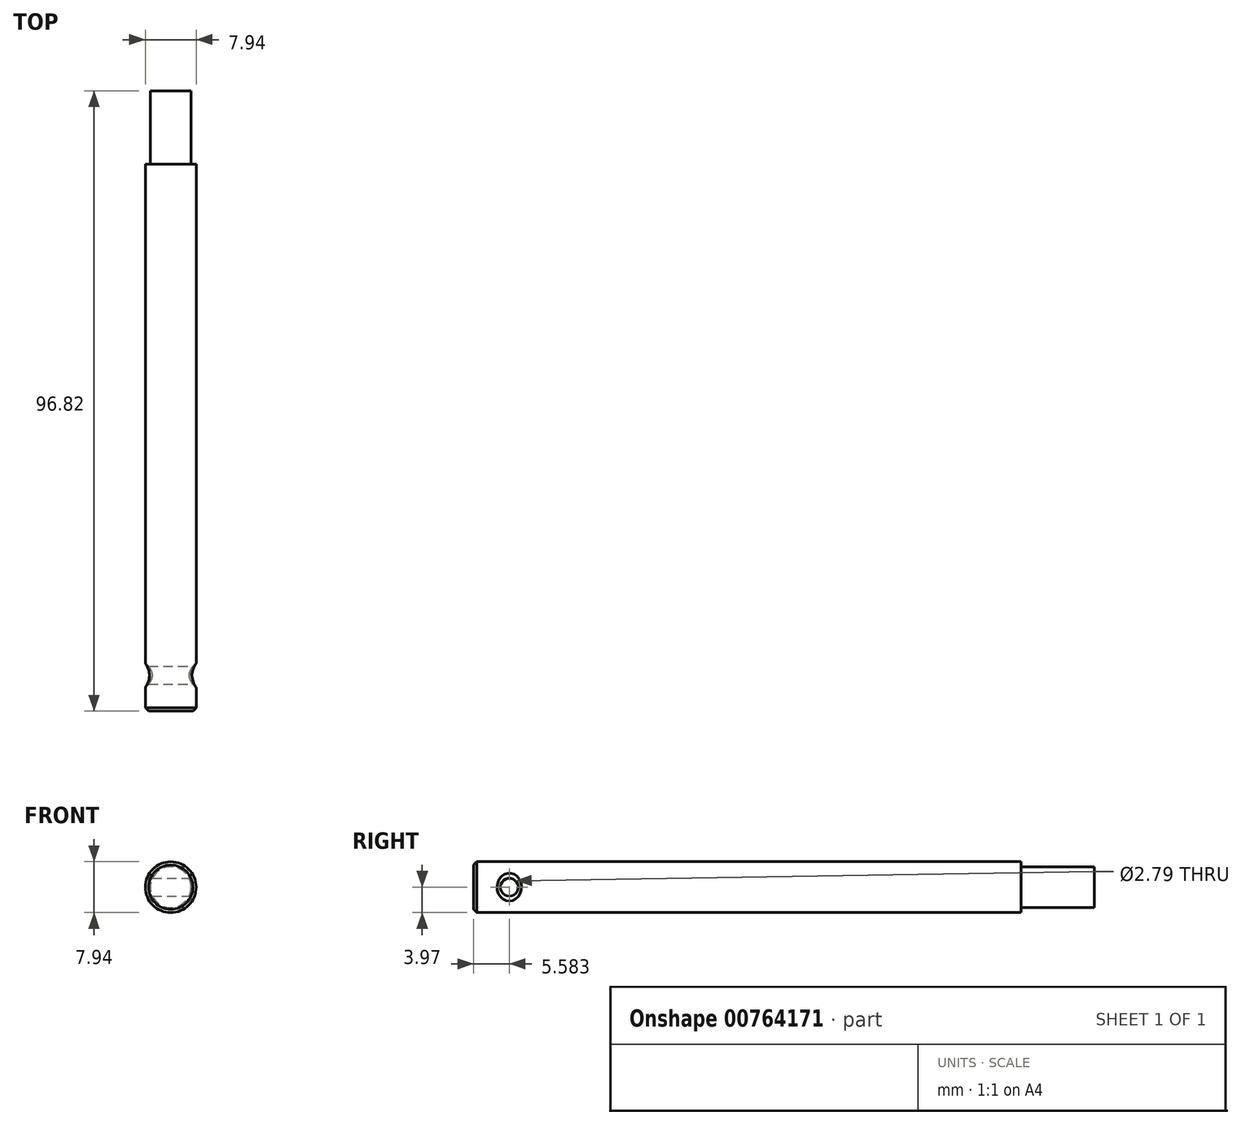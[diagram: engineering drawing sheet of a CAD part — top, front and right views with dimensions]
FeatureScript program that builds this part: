
annotation { "Feature Type Name" : "Feature", "Feature Type Description" : "" }
export const myFeature = defineFeature(function(context is Context, id is Id, definition is map)
    precondition{}
    {
        {
            var Q0;
            Q0=qCreatedBy(makeId("Front.planeOp"),FACE);
            var sketch = newSketch(context, id + "F0", { "sketchPlane" : qUnion([Q0])});
            skCircle(sketch, "E0", {"center": v(0, 0) * mm, "radius": 3.97 * mm});
            skSolve(sketch);
        }
        {
            var Q0;
            Q0=qSketchRegion(id+"F0",true);
            extrude(context, id + "F1", {"entities" : qUnion([Q0]), "depth" : 85.4 * mm});
        }
        {
            var Q0;
            Q0=makeQuery(id+"F1.opExtrude","CAP_FACE",FACE,{"disambiguationData":[OSD([sQuery(id+"F0.wireOp",EDGE,"E0")])],"isStart":true});
            var sketch = newSketch(context, id + "F2", { "sketchPlane" : qUnion([Q0])});
            skCircle(sketch, "E1", {"center": v(0, 0) * mm, "radius": 3.18 * mm});
            skSolve(sketch);
        }
        {
            var Q0;
            Q0=makeQuery(id+"F2.imprint","IMPRINT",FACE,{"disambiguationData":[TD([[makeQuery(id+"F2.imprint","IMPRINT",EDGE,{"derivedFrom":sQuery(id+"F2.wireOp",EDGE,"E1")}),1.0]])]});
            extrude(context, id + "F3", {"entities" : qUnion([Q0]), "operationType" : NewBodyOperationType.ADD, "depth" : 11.43 * mm});
        }
        {
            var Q0;
            Q0=qCreatedBy(makeId("Right.planeOp"),FACE);
            var sketch = newSketch(context, id + "F4", { "sketchPlane" : qUnion([Q0])});
            skCircle(sketch, "E2", {"center": v(-105.18, 0) * mm, "radius": 1.4 * mm});
            skCircle(sketch, "E3", {"center": v(-79.8, 0) * mm, "radius": 1.4 * mm});
            skSolve(sketch);
        }
        {
            var Q0;
            Q0=qSketchRegion(id+"F4",true);
            extrude(context, id + "F5", {"entities" : qUnion([Q0]), "operationType" : NewBodyOperationType.REMOVE, "endBound" : BoundingType.SYMMETRIC, "oppositeDirection" : true, "depth" : 25.4 * mm});
        }
        {
            var Q0;
            Q0=makeQuery(id+"F5.boolean.opBoolean","INTERSECT",EDGE,{"disambiguationData":[OD(0.0)],"derivedFrom":[makeQuery(id+"F1.opExtrude","SWEPT_FACE",FACE,{"disambiguationData":[OSD([sQuery(id+"F0.wireOp",EDGE,"E0")])]}),makeQuery(id+"F5.opExtrude","SWEPT_FACE",FACE,{"disambiguationData":[OSD([sQuery(id+"F4.wireOp",EDGE,"E3")])]})]});
            var Q1;
            Q1=makeQuery(id+"F5.boolean.opBoolean","INTERSECT",EDGE,{"disambiguationData":[OD(1.0)],"derivedFrom":[makeQuery(id+"F1.opExtrude","SWEPT_FACE",FACE,{"disambiguationData":[OSD([sQuery(id+"F0.wireOp",EDGE,"E0")])]}),makeQuery(id+"F5.opExtrude","SWEPT_FACE",FACE,{"disambiguationData":[OSD([sQuery(id+"F4.wireOp",EDGE,"E3")])]})]});
            chamfer(context, id + "F6", {"entities" : qUnion([Q0, Q1]), "width" : 0.5 * mm, "tangentPropagation" : true});
        }
        {
            var Q0;
            Q0=makeQuery(id+"F1.opExtrude","CAP_EDGE",EDGE,{"disambiguationData":[OSD([sQuery(id+"F0.wireOp",EDGE,"E0")])],"isStart":false});
            chamfer(context, id + "F7", {"entities" : qUnion([Q0]), "width" : 0.5 * mm, "tangentPropagation" : true});
        }
    });
